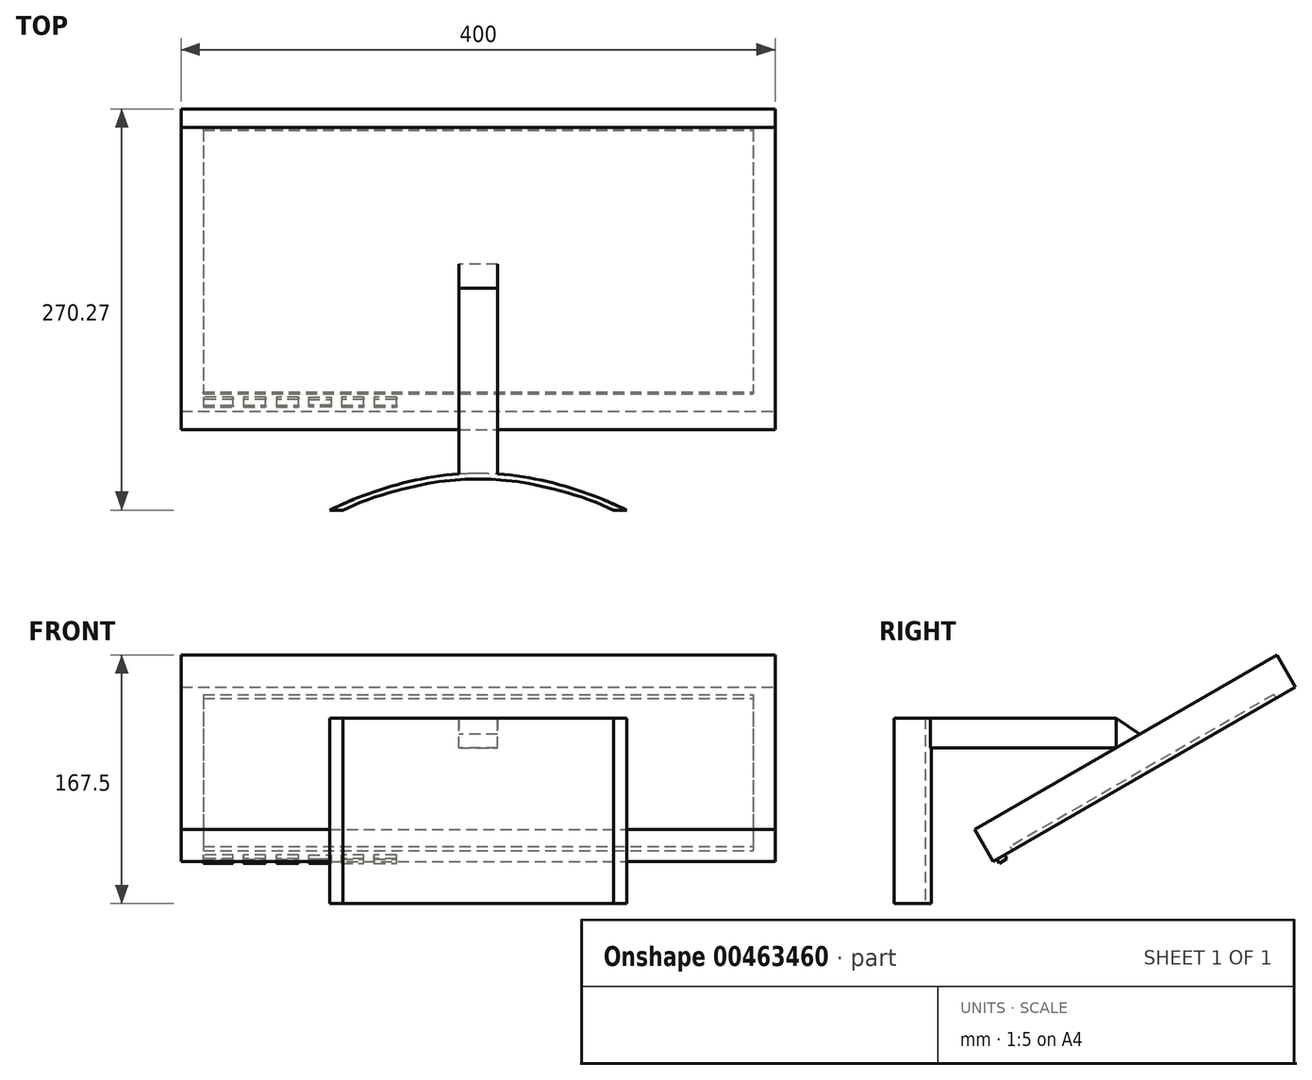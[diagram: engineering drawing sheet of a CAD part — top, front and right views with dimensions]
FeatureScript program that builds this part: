
annotation { "Feature Type Name" : "Feature", "Feature Type Description" : "" }
export const myFeature = defineFeature(function(context is Context, id is Id, definition is map)
    precondition{}
    {
        {
            var Q0;
            Q0=qCreatedBy(makeId("Top.planeOp"),FACE);
            var sketch = newSketch(context, id + "F0", { "sketchPlane" : qUnion([Q0])});
            skLineSegment(sketch, "E0", {"start": v(0, 0) * mm, "end": v(0, -50) * mm});
            skLineSegment(sketch, "E1", {"start": v(0, -50) * mm, "end": v(100, -50) * mm});
            skLineSegment(sketch, "E2", {"start": v(0, -50) * mm, "end": v(-100, -50) * mm});
            skFitSpline(sketch, "E3", {"points": [v(-100, -50) * mm, v(0, -25) * mm, v(100, -50) * mm], "startDerivative": vector(150, 75) * mm, "endDerivative": vector(150, -75) * mm});
            skFitSpline(sketch, "E4.0", {"points": [v(-98.21, -53.58) * mm, v(-92.08, -50.51) * mm, v(-78.25, -44.36) * mm, v(-58.05, -37.63) * mm, v(-40.76, -33.4) * mm, v(-27.38, -30.96) * mm, v(-16.02, -29.64) * mm, v(-6.87, -29.1) * mm, v(0, -28.95) * mm, v(6.87, -29.1) * mm, v(16.02, -29.64) * mm, v(27.38, -30.96) * mm, v(40.76, -33.4) * mm, v(58.05, -37.63) * mm, v(78.25, -44.36) * mm, v(92.08, -50.51) * mm, v(98.21, -53.58) * mm]});
            skSolve(sketch);
        }
        {
            var Q0;
            {var subQ0=sQuery(id+"F0.wireOp",EDGE,"E3");var subQ1=sQuery(id+"F0.wireOp",EDGE,"E0");var subQ2=makeQuery(id+"F0.imprint","INTERSECT",VERTEX,{"derivedFrom":[subQ1,subQ0]});Q0=makeQuery(id+"F0.imprint","IMPRINT",FACE,{"disambiguationData":[TD([[makeQuery(id+"F0.imprint","IMPRINT",EDGE,{"disambiguationData":[TD([[subQ2,-1.0]])],"derivedFrom":subQ1}),-1.0]])]});}
            var Q1;
            {var subQ0=sQuery(id+"F0.wireOp",EDGE,"E3");var subQ1=sQuery(id+"F0.wireOp",EDGE,"E0");var subQ2=makeQuery(id+"F0.imprint","INTERSECT",VERTEX,{"derivedFrom":[subQ1,subQ0]});Q1=makeQuery(id+"F0.imprint","IMPRINT",FACE,{"disambiguationData":[TD([[makeQuery(id+"F0.imprint","IMPRINT",EDGE,{"disambiguationData":[TD([[subQ2,-1.0]])],"derivedFrom":subQ1}),1.0]])]});}
            extrude(context, id + "F1", {"entities" : qUnion([Q0, Q1]), "depth" : 125 * mm});
        }
        {
            var Q0;
            Q0=makeQuery(id+"F1.opExtrude","CAP_FACE",FACE,{"disambiguationData":[OSD([sQuery(id+"F0.wireOp",EDGE,"E1"),sQuery(id+"F0.wireOp",EDGE,"E2"),sQuery(id+"F0.wireOp",EDGE,"E3"),sQuery(id+"F0.wireOp",EDGE,"E4.0")])],"isStart":false});
            var sketch = newSketch(context, id + "F2", { "sketchPlane" : qUnion([Q0])});
            skLineSegment(sketch, "E5", {"start": v(0, 0) * mm, "end": v(0, -25) * mm});
            skLineSegment(sketch, "E6", {"start": v(0, 0) * mm, "end": v(-13, 0) * mm});
            skLineSegment(sketch, "E7", {"start": v(-13, 0) * mm, "end": v(-13, -25.48) * mm});
            skLineSegment(sketch, "E8", {"start": v(13.04, 0.58) * mm, "end": v(13.04, -25.49) * mm});
            skLineSegment(sketch, "E9", {"start": v(-13, 0) * mm, "end": v(-13, 99.51) * mm});
            skLineSegment(sketch, "E10", {"start": v(-13, 99.51) * mm, "end": v(13.04, 99.51) * mm});
            skLineSegment(sketch, "E11", {"start": v(13.04, 99.51) * mm, "end": v(13.04, 0.58) * mm});
            skSolve(sketch);
        }
        {
            var Q0;
            {var subQ1=sQuery(id+"F2.wireOp",EDGE,"E5");Q0=makeQuery(id+"F2.imprint","IMPRINT",FACE,{"disambiguationData":[TD([[makeQuery(id+"F2.imprint","IMPRINT",EDGE,{"derivedFrom":subQ1}),1.0]])]});}
            var Q1;
            {var subQ0=sQuery(id+"F2.wireOp",EDGE,"E5");Q1=makeQuery(id+"F2.imprint","IMPRINT",FACE,{"disambiguationData":[TD([[makeQuery(id+"F2.imprint","IMPRINT",EDGE,{"derivedFrom":subQ0}),-1.0]])]});}
            extrude(context, id + "F3", {"entities" : qUnion([Q0, Q1]), "operationType" : NewBodyOperationType.ADD, "oppositeDirection" : true, "depth" : 20 * mm});
        }
        {
            var Q0;
            Q0=makeQuery(id+"F3.opExtrude","SWEPT_FACE",FACE,{"disambiguationData":[OSD([sQuery(id+"F2.wireOp",EDGE,"E7"),sQuery(id+"F2.wireOp",EDGE,"E9")])]});
            var sketch = newSketch(context, id + "F4", { "sketchPlane" : qUnion([Q0])});
            skLineSegment(sketch, "E12", {"start": v(25.48, 105) * mm, "end": v(-99.51, 105) * mm});
            skLineSegment(sketch, "E13", {"start": v(-99.51, 105) * mm, "end": v(-4.25, 50) * mm});
            skLineSegment(sketch, "E14", {"start": v(-99.51, 105) * mm, "end": v(-207.77, 167.5) * mm});
            skLineSegment(sketch, "E15", {"start": v(-207.77, 167.5) * mm, "end": v(-220.27, 145.85) * mm});
            skLineSegment(sketch, "E16", {"start": v(-220.27, 145.85) * mm, "end": v(-16.75, 28.35) * mm});
            skLineSegment(sketch, "E17", {"start": v(-4.25, 50) * mm, "end": v(-16.75, 28.35) * mm});
            skSolve(sketch);
        }
        {
            var Q0;
            Q0=makeQuery(id+"F4.imprint","IMPRINT",FACE,{"disambiguationData":[TD([[makeQuery(id+"F4.imprint","IMPRINT",EDGE,{"derivedFrom":sQuery(id+"F4.wireOp",EDGE,"E13")}),-1.0]])]});
            extrude(context, id + "F5", {"entities" : qUnion([Q0]), "depth" : 187 * mm});
        }
        {
            var Q0;
            Q0=makeQuery(id+"F5.opExtrude","CAP_FACE",FACE,{"disambiguationData":[OSD([sQuery(id+"F4.wireOp",EDGE,"E13"),sQuery(id+"F4.wireOp",EDGE,"E14"),sQuery(id+"F4.wireOp",EDGE,"E15"),sQuery(id+"F4.wireOp",EDGE,"E16"),sQuery(id+"F4.wireOp",EDGE,"E17")])],"isStart":true});
            var sketch = newSketch(context, id + "F6", { "sketchPlane" : qUnion([Q0])});
            skLineSegment(sketch, "E18", {"start": v(207.77, 167.5) * mm, "end": v(220.27, 145.85) * mm});
            skLineSegment(sketch, "E19", {"start": v(220.27, 145.85) * mm, "end": v(16.75, 28.35) * mm});
            skLineSegment(sketch, "E20", {"start": v(16.75, 28.35) * mm, "end": v(4.25, 50) * mm});
            skLineSegment(sketch, "E21", {"start": v(4.25, 50) * mm, "end": v(207.77, 167.5) * mm});
            skSolve(sketch);
        }
        {
            var Q0;
            Q0 = qSketchRegion(id + "F6", true);
            extrude(context, id + "F7", {"entities" : qUnion([Q0]), "operationType" : NewBodyOperationType.ADD, "depth" : 213 * mm});
        }
        {
            var Q0;
            Q0=makeQuery(id+"F7.boolean.opBoolean","MERGE",FACE,{"derivedFrom":[makeQuery(id+"F5.opExtrude","SWEPT_FACE",FACE,{"disambiguationData":[OSD([sQuery(id+"F4.wireOp",EDGE,"E16")])]}),makeQuery(id+"F7.opExtrude","SWEPT_FACE",FACE,{"disambiguationData":[OSD([sQuery(id+"F6.wireOp",EDGE,"E19")])]})]});
            var sketch = newSketch(context, id + "F8", { "sketchPlane" : qUnion([Q0])});
            skLineSegment(sketch, "E22.0", {"start": v(-185, -43.68) * mm, "end": v(185, -43.68) * mm});
            skLineSegment(sketch, "E22.1", {"start": v(-185, -248.68) * mm, "end": v(-185, -43.68) * mm});
            skLineSegment(sketch, "E22.2", {"start": v(-185, -248.68) * mm, "end": v(185, -248.68) * mm});
            skLineSegment(sketch, "E22.3", {"start": v(185, -248.68) * mm, "end": v(185, -43.68) * mm});
            skSolve(sketch);
        }
        {
            var Q0;
            Q0 = qSketchRegion(id + "F8", true);
            extrude(context, id + "F9", {"entities" : qUnion([Q0]), "operationType" : NewBodyOperationType.REMOVE, "oppositeDirection" : true, "depth" : 3 * mm});
        }
        {
            var Q0;
            Q0=makeQuery(id+"F7.boolean.opBoolean","MERGE",FACE,{"derivedFrom":[makeQuery(id+"F5.opExtrude","SWEPT_FACE",FACE,{"disambiguationData":[OSD([sQuery(id+"F4.wireOp",EDGE,"E16")])]}),makeQuery(id+"F7.opExtrude","SWEPT_FACE",FACE,{"disambiguationData":[OSD([sQuery(id+"F6.wireOp",EDGE,"E19")])]})]});
            var sketch = newSketch(context, id + "F10", { "sketchPlane" : qUnion([Q0])});
            skLineSegment(sketch, "E23", {"start": v(-185, -28.68) * mm, "end": v(-185, -31.68) * mm});
            skLineSegment(sketch, "E24", {"start": v(-185, -31.68) * mm, "end": v(-200, -31.68) * mm});
            skLineSegment(sketch, "E25", {"start": v(-185, -43.68) * mm, "end": v(-185, -37.68) * mm});
            skLineSegment(sketch, "E26", {"start": v(-185, -37.68) * mm, "end": v(-185, -31.68) * mm});
            skLineSegment(sketch, "E27", {"start": v(-185, -31.68) * mm, "end": v(-165, -31.68) * mm});
            skLineSegment(sketch, "E28", {"start": v(-165, -31.68) * mm, "end": v(-165, -37.68) * mm});
            skLineSegment(sketch, "E29", {"start": v(-165, -37.68) * mm, "end": v(-185, -37.68) * mm});
            skLineSegment(sketch, "E30", {"start": v(-165, -37.68) * mm, "end": v(-158, -37.68) * mm});
            skLineSegment(sketch, "E31", {"start": v(-158, -37.68) * mm, "end": v(-158, -31.68) * mm});
            skLineSegment(sketch, "E32", {"start": v(-158, -31.68) * mm, "end": v(-143, -31.68) * mm});
            skLineSegment(sketch, "E33", {"start": v(-143, -31.68) * mm, "end": v(-143, -37.68) * mm});
            skLineSegment(sketch, "E34", {"start": v(-143, -37.68) * mm, "end": v(-158, -37.68) * mm});
            skLineSegment(sketch, "E35", {"start": v(-143, -37.68) * mm, "end": v(-136, -37.68) * mm});
            skLineSegment(sketch, "E36", {"start": v(-136, -37.68) * mm, "end": v(-136, -31.68) * mm});
            skLineSegment(sketch, "E37", {"start": v(-136, -31.68) * mm, "end": v(-121, -31.68) * mm});
            skLineSegment(sketch, "E38", {"start": v(-121, -31.68) * mm, "end": v(-121, -37.68) * mm});
            skLineSegment(sketch, "E39", {"start": v(-121, -37.68) * mm, "end": v(-136, -37.68) * mm});
            skLineSegment(sketch, "E40", {"start": v(-121, -37.68) * mm, "end": v(-114, -37.68) * mm});
            skLineSegment(sketch, "E41", {"start": v(-114, -37.68) * mm, "end": v(-99, -37.68) * mm});
            skLineSegment(sketch, "E42", {"start": v(-99, -37.68) * mm, "end": v(-99, -31.68) * mm});
            skLineSegment(sketch, "E43", {"start": v(-99, -31.68) * mm, "end": v(-114, -31.68) * mm});
            skLineSegment(sketch, "E44", {"start": v(-114, -31.68) * mm, "end": v(-114, -37.68) * mm});
            skLineSegment(sketch, "E45", {"start": v(-99, -37.68) * mm, "end": v(-92, -37.68) * mm});
            skLineSegment(sketch, "E46", {"start": v(-92, -37.68) * mm, "end": v(-92, -31.68) * mm});
            skLineSegment(sketch, "E47", {"start": v(-92, -31.68) * mm, "end": v(-77, -31.68) * mm});
            skLineSegment(sketch, "E48", {"start": v(-77, -31.68) * mm, "end": v(-77, -37.68) * mm});
            skLineSegment(sketch, "E49", {"start": v(-77, -37.68) * mm, "end": v(-92, -37.68) * mm});
            skLineSegment(sketch, "E50", {"start": v(-77, -37.68) * mm, "end": v(-70, -37.68) * mm});
            skLineSegment(sketch, "E51", {"start": v(-70, -37.68) * mm, "end": v(-70, -31.68) * mm});
            skLineSegment(sketch, "E52", {"start": v(-70, -31.68) * mm, "end": v(-55, -31.68) * mm});
            skLineSegment(sketch, "E53", {"start": v(-55, -31.68) * mm, "end": v(-55, -37.68) * mm});
            skLineSegment(sketch, "E54", {"start": v(-55, -37.68) * mm, "end": v(-70, -37.68) * mm});
            skSolve(sketch);
        }
        {
            var Q0;
            Q0 = qSketchRegion(id + "F10", true);
            extrude(context, id + "F11", {"entities" : qUnion([Q0]), "operationType" : NewBodyOperationType.ADD, "depth" : 3 * mm});
        }
        {
            var Q0;
            Q0=makeQuery(id+"F3.opExtrude","SWEPT_FACE",FACE,{"disambiguationData":[OSD([sQuery(id+"F2.wireOp",EDGE,"E7"),sQuery(id+"F2.wireOp",EDGE,"E9")])]});
            var sketch = newSketch(context, id + "F12", { "sketchPlane" : qUnion([Q0])});
            skLineSegment(sketch, "E55", {"start": v(-99.51, 125) * mm, "end": v(-99.51, 105) * mm});
            skPoint(sketch, "E56.end.orphan", {"position": v(-108.94, 125) * mm});
            skPoint(sketch, "E57.start.orphan", {"position": v(-108.94, 105) * mm});
            skLineSegment(sketch, "E58", {"start": v(-99.51, 125) * mm, "end": v(-129.51, 105) * mm});
            skLineSegment(sketch, "E59", {"start": v(-99.51, 105) * mm, "end": v(-115.8, 114.15) * mm});
            skSolve(sketch);
        }
        {
            var Q0;
            {var subQ0=sQuery(id+"F12.wireOp",EDGE,"E55");Q0=makeQuery(id+"F12.imprint","IMPRINT",FACE,{"disambiguationData":[TD([[makeQuery(id+"F12.imprint","IMPRINT",EDGE,{"derivedFrom":subQ0}),1.0]])]});}
            extrude(context, id + "F13", {"entities" : qUnion([Q0]), "oppositeDirection" : true, "depth" : 26 * mm});
        }
    });
